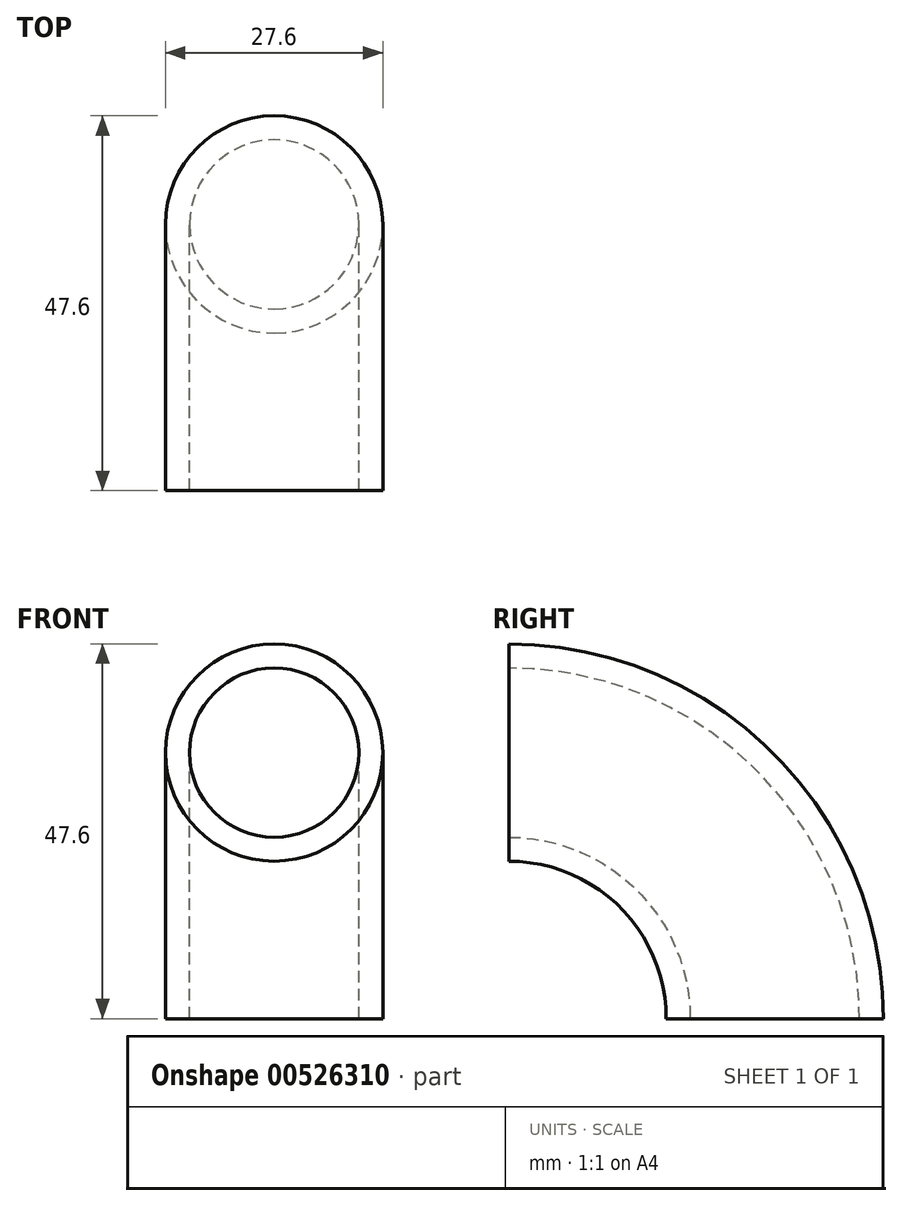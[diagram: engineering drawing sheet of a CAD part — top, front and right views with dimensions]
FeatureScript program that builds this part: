
annotation { "Feature Type Name" : "Feature", "Feature Type Description" : "" }
export const myFeature = defineFeature(function(context is Context, id is Id, definition is map)
    precondition{}
    {
        {
            var Q0;
            Q0=qCreatedBy(makeId("Front.planeOp"),FACE);
            var sketch = newSketch(context, id + "F0", { "sketchPlane" : qUnion([Q0])});
            skCircle(sketch, "E0", {"center": v(0, 0) * mm, "radius": 10.75 * mm});
            skCircle(sketch, "E1", {"center": v(0, 0) * mm, "radius": 13.8 * mm});
            skSolve(sketch);
        }
        {
            var Q0;
            Q0=qCreatedBy(makeId("Right.planeOp"),FACE);
            var sketch = newSketch(context, id + "F1", { "sketchPlane" : qUnion([Q0])});
            skPoint(sketch, "E2", {"position": v(0, -33.8) * mm});
            skLineSegment(sketch, "E3", {"start": v(0, -33.8) * mm, "end": v(61.34, -33.8) * mm, "construction": true});
            skArc(sketch, "E4", {"start": v(0, 0) * mm, "mid": v(23.9, -9.9) * mm, "end": v(33.8, -33.8) * mm});
            skSolve(sketch);
        }
        {
            var Q0;
            Q0=makeQuery(id+"F0.imprint","IMPRINT",FACE,{"disambiguationData":[TD([[makeQuery(id+"F0.imprint","IMPRINT",EDGE,{"derivedFrom":sQuery(id+"F0.wireOp",EDGE,"E0")}),-1.0]])]});
            var Q1;
            Q1=sQuery(id+"F1.wireOp",EDGE,"E4");
            sweep(context, id + "F2", {"profiles" : qUnion([Q0]), "path" : qUnion([Q1])});
        }
    });
